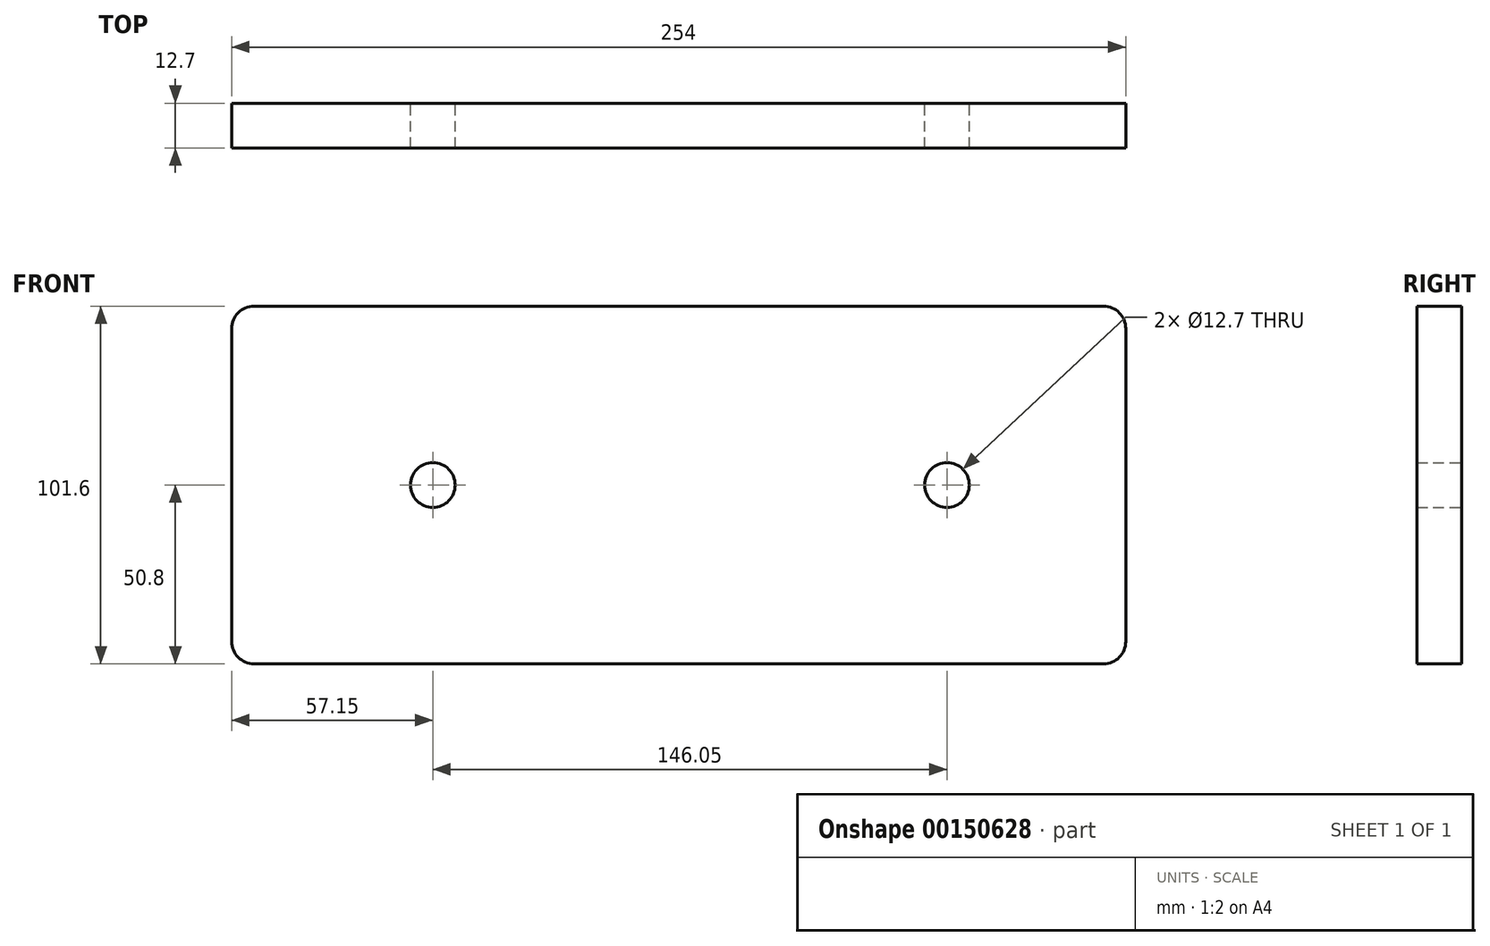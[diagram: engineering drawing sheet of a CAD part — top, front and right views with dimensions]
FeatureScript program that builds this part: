
annotation { "Feature Type Name" : "Feature", "Feature Type Description" : "" }
export const myFeature = defineFeature(function(context is Context, id is Id, definition is map)
    precondition{}
    {
        {
            var Q0;
            Q0=qCreatedBy(makeId("Front.planeOp"),FACE);
            var sketch = newSketch(context, id + "F0", { "sketchPlane" : qUnion([Q0])});
            skLineSegment(sketch, "E0.bottom", {"start": v(0, 0) * mm, "end": v(254, 0) * mm});
            skLineSegment(sketch, "E0.top", {"start": v(0, 101.6) * mm, "end": v(254, 101.6) * mm});
            skLineSegment(sketch, "E0.left", {"start": v(0, 0) * mm, "end": v(0, 101.6) * mm});
            skLineSegment(sketch, "E0.right", {"start": v(254, 0) * mm, "end": v(254, 101.6) * mm});
            skCircle(sketch, "E1", {"center": v(57.15, 50.8) * mm, "radius": 6.35 * mm});
            skPoint(sketch, "E1.centerSnap0", {"position": v(0, 50.8) * mm});
            skCircle(sketch, "E2", {"center": v(203.2, 50.8) * mm, "radius": 6.35 * mm});
            skPoint(sketch, "E2.centerSnap0", {"position": v(254, 50.8) * mm});
            skSolve(sketch);
        }
        {
            var Q0;
            Q0 = qSketchRegion(id + "F0", true);
            extrude(context, id + "F1", {"entities" : qUnion([Q0]), "depth" : 12.7 * mm});
        }
        {
            var Q0;
            Q0=makeQuery(id+"F1.opExtrude","SWEPT_EDGE",EDGE,{"disambiguationData":[OSD([sQuery(id+"F0.wireOp",EDGE,"E0.top"),sQuery(id+"F0.wireOp",EDGE,"E0.left")])]});
            var Q1;
            Q1=makeQuery(id+"F1.opExtrude","SWEPT_EDGE",EDGE,{"disambiguationData":[OSD([sQuery(id+"F0.wireOp",EDGE,"E0.bottom"),sQuery(id+"F0.wireOp",EDGE,"E0.left")])]});
            var Q2;
            Q2=makeQuery(id+"F1.opExtrude","SWEPT_EDGE",EDGE,{"disambiguationData":[OSD([sQuery(id+"F0.wireOp",EDGE,"E0.bottom"),sQuery(id+"F0.wireOp",EDGE,"E0.right")])]});
            var Q3;
            Q3=makeQuery(id+"F1.opExtrude","SWEPT_EDGE",EDGE,{"disambiguationData":[OSD([sQuery(id+"F0.wireOp",EDGE,"E0.top"),sQuery(id+"F0.wireOp",EDGE,"E0.right")])]});
            fillet(context, id + "F2", {"entities" : qUnion([Q0, Q1, Q2, Q3]), "radius" : 6.35 * mm, "tangentPropagation" : true, "allowEdgeOverflow" : false});
        }
    });
